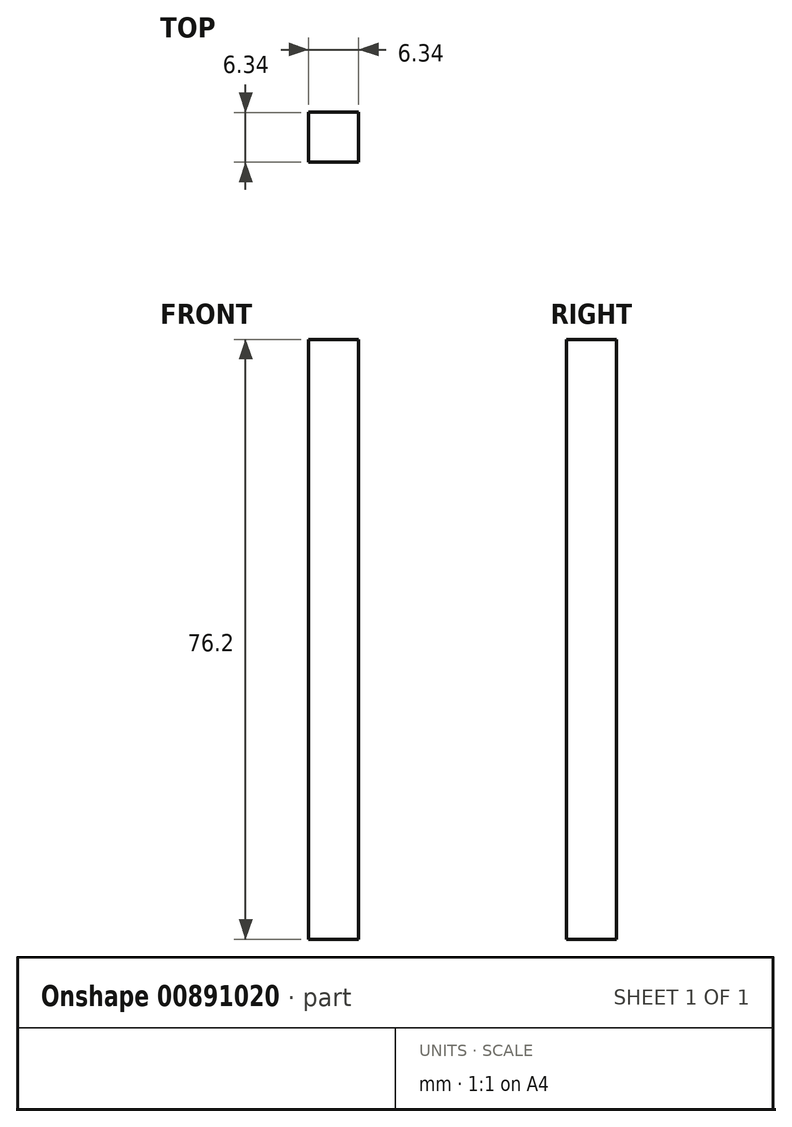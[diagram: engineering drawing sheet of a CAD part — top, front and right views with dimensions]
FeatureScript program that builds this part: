
annotation { "Feature Type Name" : "Feature", "Feature Type Description" : "" }
export const myFeature = defineFeature(function(context is Context, id is Id, definition is map)
    precondition{}
    {
        {
            var Q0;
            Q0=qCreatedBy(makeId("Top.planeOp"),FACE);
            var sketch = newSketch(context, id + "F0", { "sketchPlane" : qUnion([Q0])});
            skLineSegment(sketch, "E0.bottom", {"start": v(3.17, -3.18) * mm, "end": v(-3.18, -3.18) * mm});
            skLineSegment(sketch, "E0.top", {"start": v(3.17, 3.17) * mm, "end": v(-3.18, 3.17) * mm});
            skLineSegment(sketch, "E0.left", {"start": v(3.17, -3.18) * mm, "end": v(3.17, 3.17) * mm});
            skLineSegment(sketch, "E0.right", {"start": v(-3.18, -3.18) * mm, "end": v(-3.18, 3.17) * mm});
            skPoint(sketch, "E0.middle", {"position": v(0, 0) * mm});
            skSolve(sketch);
        }
        {
            var Q0;
            Q0 = qSketchRegion(id + "F0", true);
            extrude(context, id + "F1", {"entities" : qUnion([Q0]), "depth" : 76.2 * mm, "offsetDistance" : 25.4 * mm});
        }
    });
